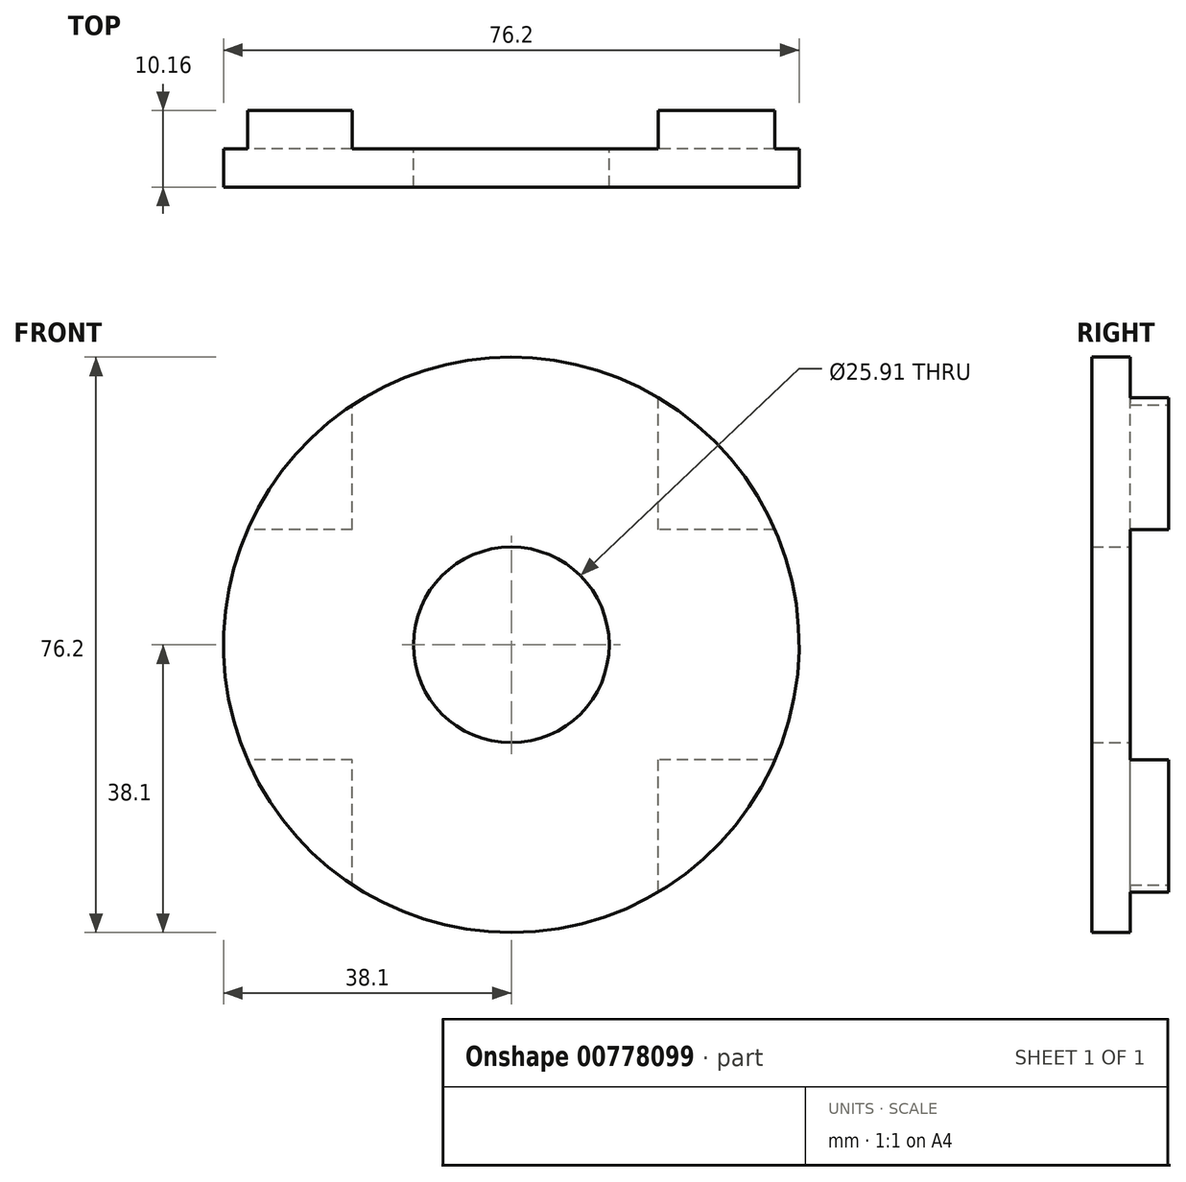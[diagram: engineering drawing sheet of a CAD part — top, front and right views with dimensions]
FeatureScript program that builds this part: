
annotation { "Feature Type Name" : "Feature", "Feature Type Description" : "" }
export const myFeature = defineFeature(function(context is Context, id is Id, definition is map)
    precondition{}
    {
        {
            var Q0;
            Q0=qCreatedBy(makeId("Front.planeOp"),FACE);
            var sketch = newSketch(context, id + "F0", { "sketchPlane" : qUnion([Q0])});
            skCircle(sketch, "E0", {"center": v(0, 0) * mm, "radius": 12.7 * mm});
            skSolve(sketch);
        }
        {
            var Q0;
            Q0=qSketchRegion(id+"F0",true);
            extrude(context, id + "F1", {"entities" : qUnion([Q0]), "depth" : 17.78 * mm, "offsetDistance" : 25.4 * mm});
        }
        {
            var Q0;
            Q0=qCreatedBy(makeId("Front.planeOp"),FACE);
            var sketch = newSketch(context, id + "F2", { "sketchPlane" : qUnion([Q0])});
            skCircle(sketch, "E1", {"center": v(0, 0) * mm, "radius": 38.1 * mm});
            skSolve(sketch);
        }
        {
            var Q0;
            Q0=qSketchRegion(id+"F2",true);
            extrude(context, id + "F3", {"entities" : qUnion([Q0]), "operationType" : NewBodyOperationType.ADD, "depth" : 10.16 * mm, "offsetDistance" : 25.4 * mm});
        }
        {
            var Q0;
            Q0=qCreatedBy(makeId("Front.planeOp"),FACE);
            var sketch = newSketch(context, id + "F4", { "sketchPlane" : qUnion([Q0])});
            skCircle(sketch, "E2", {"center": v(0, 0) * mm, "radius": 12.95 * mm});
            skSolve(sketch);
        }
        {
            var Q0;
            Q0=qSketchRegion(id+"F4",true);
            extrude(context, id + "F5", {"entities" : qUnion([Q0]), "operationType" : NewBodyOperationType.REMOVE, "endBound" : BoundingType.THROUGH_ALL, "depth" : 25.4 * mm, "offsetDistance" : 25.4 * mm, "hasSecondDirection" : true, "secondDirectionBound" : SecondDirectionBoundingType.THROUGH_ALL, "secondDirectionOppositeDirection" : true, "secondDirectionDepth" : 25.4 * mm});
        }
        {
            var Q0;
            Q0=qCreatedBy(makeId("Right.planeOp"),FACE);
            var sketch = newSketch(context, id + "F6", { "sketchPlane" : qUnion([Q0])});
            skLineSegment(sketch, "E3.bottom", {"start": v(0, 15.24) * mm, "end": v(-5.08, 15.24) * mm});
            skLineSegment(sketch, "E3.top", {"start": v(0, -15.24) * mm, "end": v(-5.08, -15.24) * mm});
            skLineSegment(sketch, "E3.left", {"start": v(0, 15.24) * mm, "end": v(0, -15.24) * mm});
            skLineSegment(sketch, "E3.right", {"start": v(-5.08, 15.24) * mm, "end": v(-5.08, -15.24) * mm});
            skSolve(sketch);
        }
        {
            var Q0;
            Q0 = qSketchRegion(id + "F6", true);
            extrude(context, id + "F7", {"entities" : qUnion([Q0]), "operationType" : NewBodyOperationType.REMOVE, "endBound" : BoundingType.THROUGH_ALL, "depth" : 25.4 * mm, "offsetDistance" : 25.4 * mm, "hasSecondDirection" : true, "secondDirectionBound" : SecondDirectionBoundingType.THROUGH_ALL, "secondDirectionOppositeDirection" : true, "secondDirectionDepth" : 25.4 * mm});
        }
        {
            var Q0;
            Q0=qCreatedBy(makeId("Top.planeOp"),FACE);
            var sketch = newSketch(context, id + "F8", { "sketchPlane" : qUnion([Q0])});
            skLineSegment(sketch, "E4.bottom", {"start": v(-21.04, 0) * mm, "end": v(19.47, 0) * mm});
            skLineSegment(sketch, "E4.top", {"start": v(-21.04, -5.08) * mm, "end": v(19.47, -5.08) * mm});
            skLineSegment(sketch, "E4.left", {"start": v(-21.04, 0) * mm, "end": v(-21.04, -5.08) * mm});
            skLineSegment(sketch, "E4.right", {"start": v(19.47, 0) * mm, "end": v(19.47, -5.08) * mm});
            skSolve(sketch);
        }
        {
            var Q0;
            Q0 = qSketchRegion(id + "F8", true);
            extrude(context, id + "F9", {"entities" : qUnion([Q0]), "operationType" : NewBodyOperationType.REMOVE, "endBound" : BoundingType.THROUGH_ALL, "oppositeDirection" : true, "depth" : 25.4 * mm, "offsetDistance" : 25.4 * mm, "hasSecondDirection" : true, "secondDirectionBound" : SecondDirectionBoundingType.THROUGH_ALL, "secondDirectionOppositeDirection" : false, "secondDirectionDepth" : 25.4 * mm});
        }
    });
